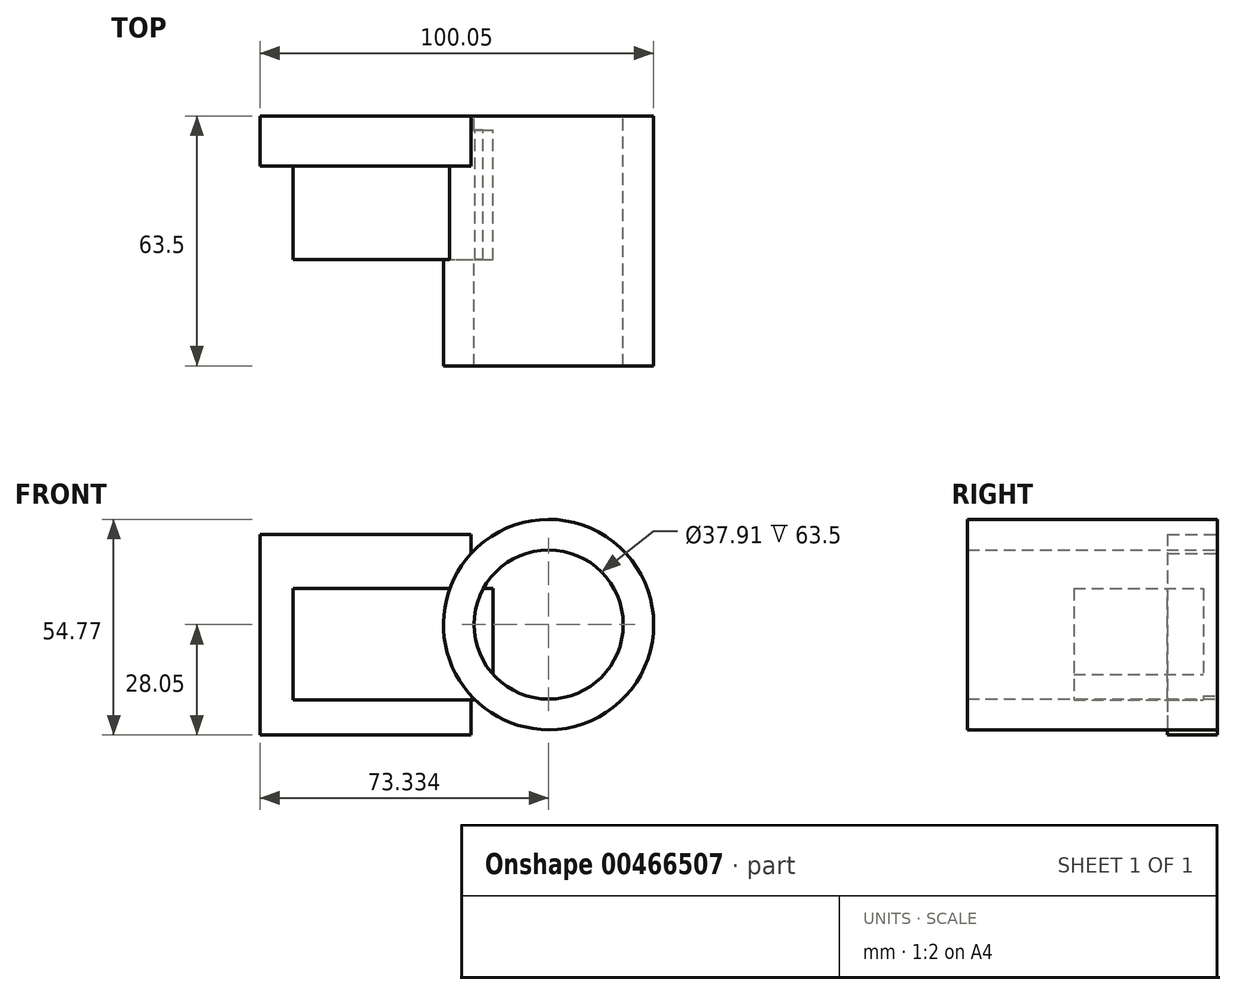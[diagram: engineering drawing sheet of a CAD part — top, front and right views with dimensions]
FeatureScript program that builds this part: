
annotation { "Feature Type Name" : "Feature", "Feature Type Description" : "" }
export const myFeature = defineFeature(function(context is Context, id is Id, definition is map)
    precondition{}
    {
        {
            var Q0;
            Q0=qCreatedBy(makeId("Front.planeOp"),FACE);
            var sketch = newSketch(context, id + "F0", { "sketchPlane" : qUnion([Q0])});
            skLineSegment(sketch, "E0.bottom", {"start": v(-59.25, 22.95) * mm, "end": v(-5.58, 22.95) * mm});
            skLineSegment(sketch, "E0.top", {"start": v(-59.25, -28.05) * mm, "end": v(-5.58, -28.05) * mm});
            skLineSegment(sketch, "E0.left", {"start": v(-59.25, 22.95) * mm, "end": v(-59.25, -28.05) * mm});
            skLineSegment(sketch, "E0.right", {"start": v(-5.58, 22.95) * mm, "end": v(-5.58, -28.05) * mm});
            skSolve(sketch);
        }
        {
            var Q0;
            Q0=qCreatedBy(makeId("Front.planeOp"),FACE);
            var sketch = newSketch(context, id + "F1", { "sketchPlane" : qUnion([Q0])});
            skCircle(sketch, "E1", {"center": v(14.08, 0) * mm, "radius": 26.72 * mm});
            skCircle(sketch, "E2", {"center": v(14.08, 0) * mm, "radius": 18.95 * mm});
            skSolve(sketch);
        }
        {
            var Q0;
            Q0 = qSketchRegion(id + "F1", true);
            extrude(context, id + "F2", {"entities" : qUnion([Q0]), "depth" : 63.5 * mm});
        }
        {
            var Q0;
            Q0=makeQuery(id+"F0.imprint","IMPRINT",FACE,{"disambiguationData":[TD([[makeQuery(id+"F0.imprint","IMPRINT",EDGE,{"derivedFrom":sQuery(id+"F0.wireOp",EDGE,"E0.bottom")}),-1.0]])]});
            extrude(context, id + "F3", {"entities" : qUnion([Q0]), "operationType" : NewBodyOperationType.ADD, "depth" : 12.7 * mm});
        }
        {
            var Q0;
            Q0=qCreatedBy(makeId("Right.planeOp"),FACE);
            var sketch = newSketch(context, id + "F4", { "sketchPlane" : qUnion([Q0])});
            skLineSegment(sketch, "E3.bottom", {"start": v(-36.53, 9.17) * mm, "end": v(-3.62, 9.17) * mm});
            skLineSegment(sketch, "E3.top", {"start": v(-36.53, -19.16) * mm, "end": v(-3.62, -19.16) * mm});
            skLineSegment(sketch, "E3.left", {"start": v(-36.53, 9.17) * mm, "end": v(-36.53, -19.16) * mm});
            skLineSegment(sketch, "E3.right", {"start": v(-3.62, 9.17) * mm, "end": v(-3.62, -19.16) * mm});
            skSolve(sketch);
        }
        {
            var Q0;
            Q0 = qSketchRegion(id + "F4", true);
            extrude(context, id + "F5", {"entities" : qUnion([Q0]), "operationType" : NewBodyOperationType.ADD, "oppositeDirection" : true, "depth" : 50.8 * mm});
        }
    });
